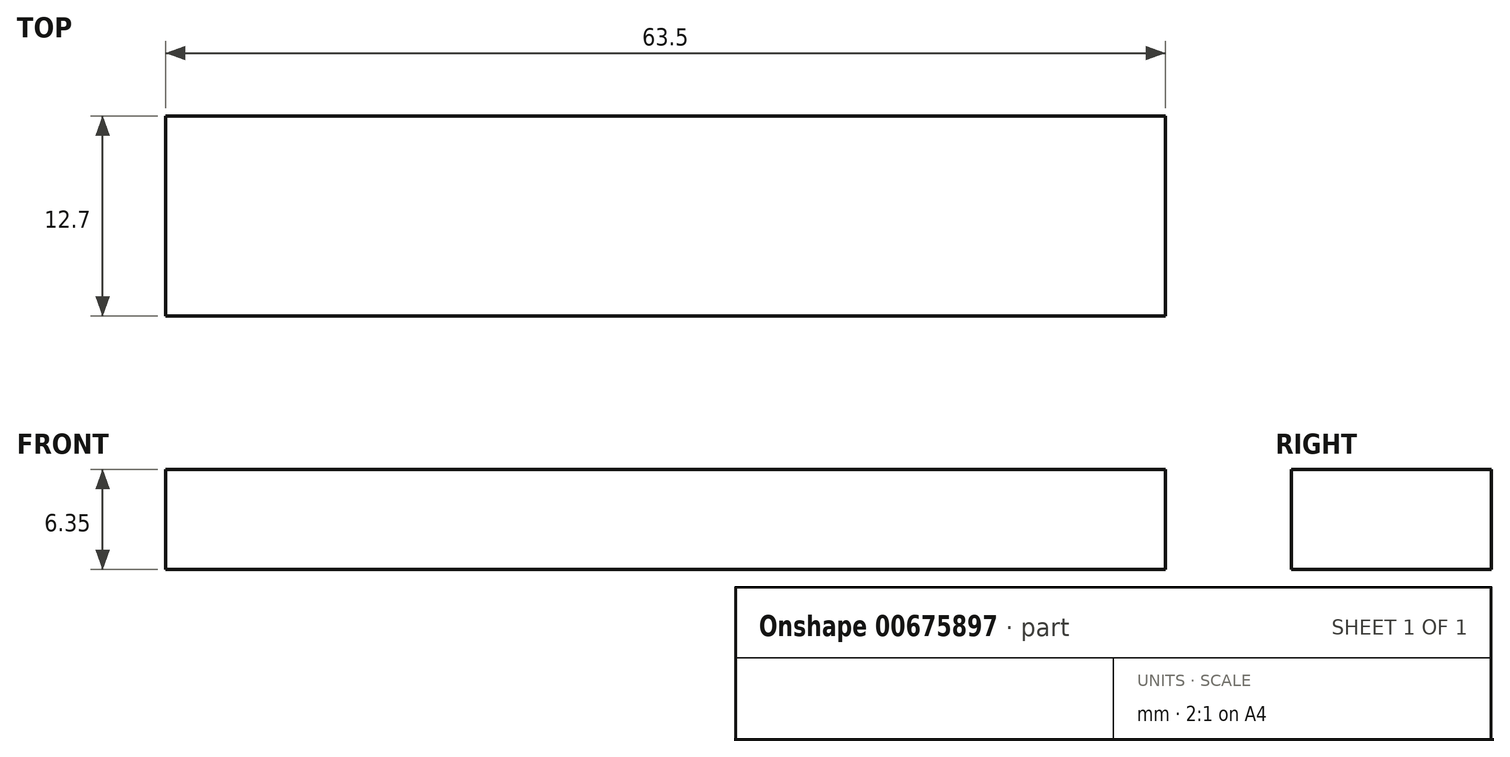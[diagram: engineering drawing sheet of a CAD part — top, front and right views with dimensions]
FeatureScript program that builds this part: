
annotation { "Feature Type Name" : "Feature", "Feature Type Description" : "" }
export const myFeature = defineFeature(function(context is Context, id is Id, definition is map)
    precondition{}
    {
        {
            var Q0;
            Q0=qCreatedBy(makeId("Top.planeOp"),FACE);
            var sketch = newSketch(context, id + "F0", { "sketchPlane" : qUnion([Q0])});
            skLineSegment(sketch, "E0.bottom", {"start": v(-61.1, 0.68) * mm, "end": v(2.4, 0.68) * mm});
            skLineSegment(sketch, "E0.top", {"start": v(-61.1, -12.02) * mm, "end": v(2.4, -12.02) * mm});
            skLineSegment(sketch, "E0.left", {"start": v(-61.1, 0.68) * mm, "end": v(-61.1, -12.02) * mm});
            skLineSegment(sketch, "E0.right", {"start": v(2.4, 0.68) * mm, "end": v(2.4, -12.02) * mm});
            skSolve(sketch);
        }
        {
            var Q0;
            Q0 = qSketchRegion(id + "F0", true);
            extrude(context, id + "F1", {"entities" : qUnion([Q0]), "depth" : 6.35 * mm, "offsetDistance" : 25.4 * mm});
        }
    });
